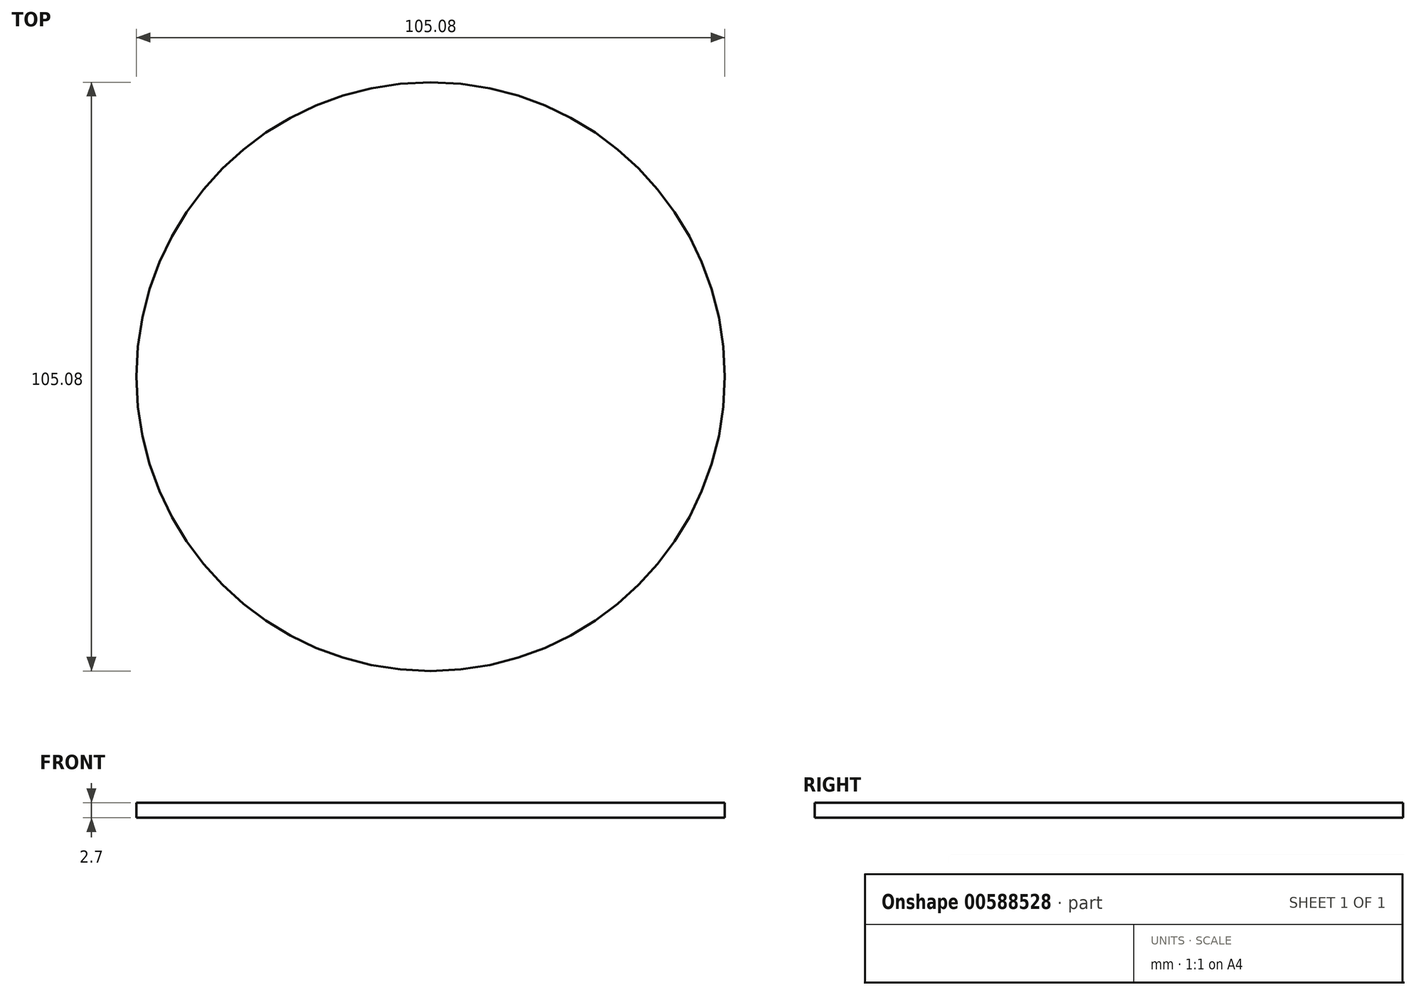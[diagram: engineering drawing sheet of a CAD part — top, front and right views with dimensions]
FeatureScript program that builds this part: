
annotation { "Feature Type Name" : "Feature", "Feature Type Description" : "" }
export const myFeature = defineFeature(function(context is Context, id is Id, definition is map)
    precondition{}
    {
        {
            var Q0;
            Q0=qCreatedBy(makeId("Top.planeOp"),FACE);
            var sketch = newSketch(context, id + "F0", { "sketchPlane" : qUnion([Q0])});
            skCircle(sketch, "E0", {"center": v(0, 0) * mm, "radius": 52.54 * mm});
            skSolve(sketch);
        }
        {
            var Q0;
            Q0 = qSketchRegion(id + "F0", true);
            extrude(context, id + "F1", {"entities" : qUnion([Q0]), "oppositeDirection" : true, "depth" : 2.7 * mm, "offsetDistance" : 25 * mm});
        }
    });
